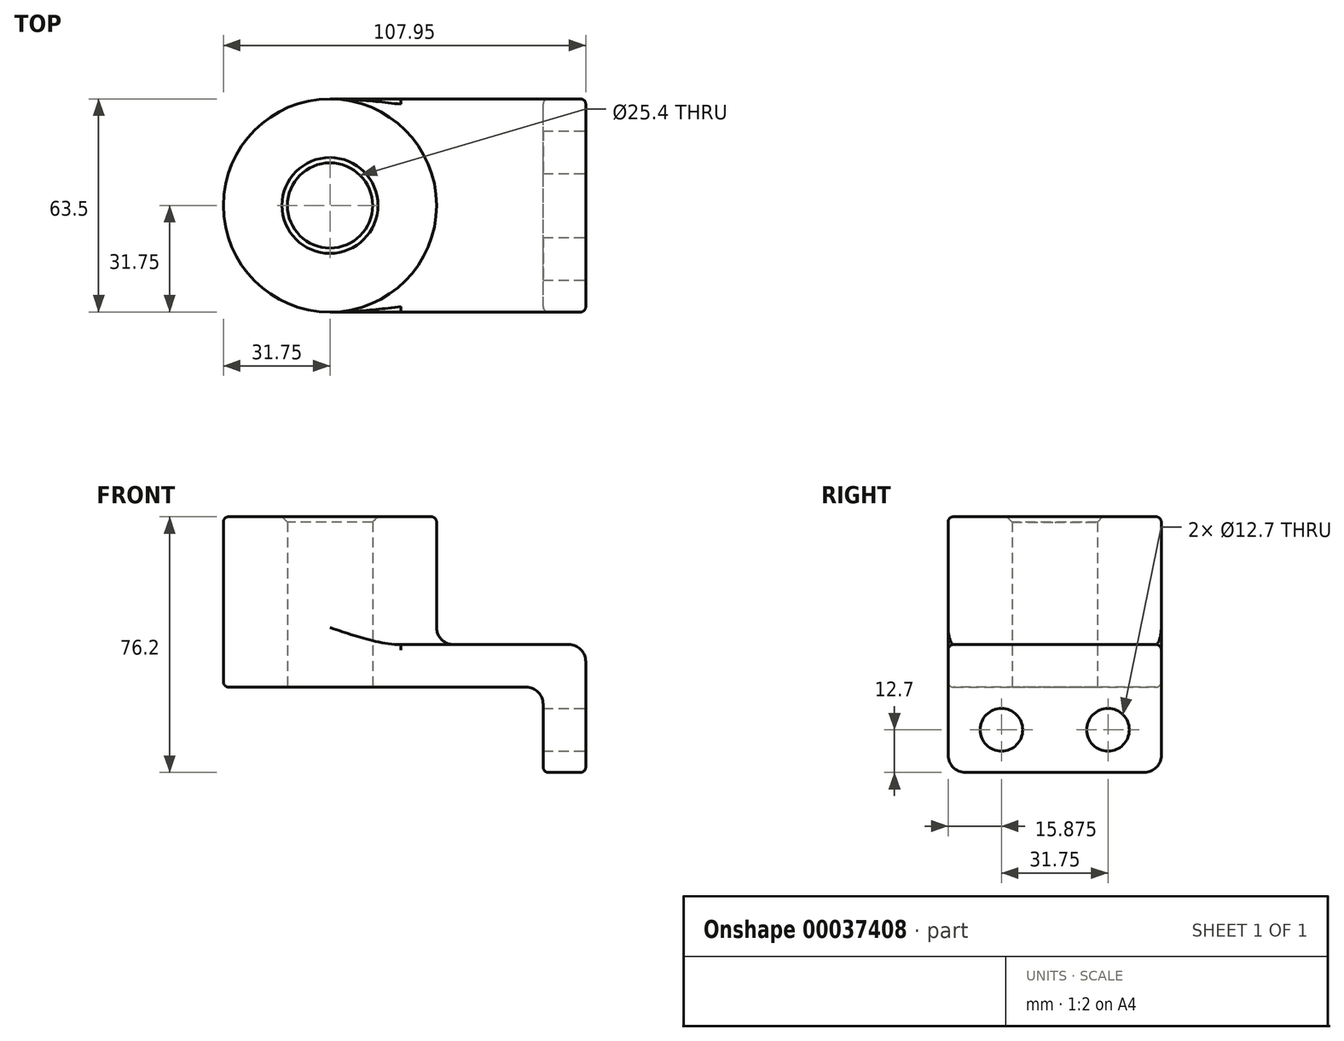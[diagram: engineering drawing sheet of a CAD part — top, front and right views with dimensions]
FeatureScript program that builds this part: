
annotation { "Feature Type Name" : "Feature", "Feature Type Description" : "" }
export const myFeature = defineFeature(function(context is Context, id is Id, definition is map)
    precondition{}
    {
        {
            var Q0;
            Q0=qCreatedBy(makeId("Top.planeOp"),FACE);
            var sketch = newSketch(context, id + "F0", { "sketchPlane" : qUnion([Q0])});
            skLineSegment(sketch, "E0.rect.bottom", {"start": v(-38.1, 31.75) * mm, "end": v(38.1, 31.75) * mm});
            skLineSegment(sketch, "E0.rect.top", {"start": v(-38.1, -31.75) * mm, "end": v(38.1, -31.75) * mm});
            skLineSegment(sketch, "E0.rect.left", {"start": v(-38.1, 31.75) * mm, "end": v(-38.1, -31.75) * mm});
            skLineSegment(sketch, "E0.rect.right", {"start": v(38.1, 31.75) * mm, "end": v(38.1, -31.75) * mm});
            skPoint(sketch, "E0.rect.middle", {"position": v(0, 0) * mm});
            skCircle(sketch, "E1", {"center": v(-38.1, 0) * mm, "radius": 31.75 * mm});
            skCircle(sketch, "E2", {"center": v(-38.1, 0) * mm, "radius": 12.7 * mm});
            skSolve(sketch);
        }
        {
            var Q0;
            {var subQ3=sQuery(id+"F0.wireOp",EDGE,"E0.rect.bottom");Q0=makeQuery(id+"F0.imprint","IMPRINT",FACE,{"disambiguationData":[TD([[makeQuery(id+"F0.imprint","IMPRINT",EDGE,{"derivedFrom":subQ3}),-1.0]])]});}
            var Q1;
            {var subQ0=sQuery(id+"F0.wireOp",EDGE,"E2");var subQ1=sQuery(id+"F0.wireOp",EDGE,"E0.rect.left");var subQ3=makeQuery(id+"F0.imprint","INTERSECT",VERTEX,{"disambiguationData":[OD(0.0)],"derivedFrom":[subQ1,subQ0]});Q1=makeQuery(id+"F0.imprint","IMPRINT",FACE,{"disambiguationData":[TD([[makeQuery(id+"F0.imprint","IMPRINT",EDGE,{"disambiguationData":[TD([[subQ3,1.0]])],"derivedFrom":subQ0}),-1.0]])]});}
            var Q2;
            {var subQ0=sQuery(id+"F0.wireOp",EDGE,"E2");var subQ1=sQuery(id+"F0.wireOp",EDGE,"E0.rect.left");var subQ3=makeQuery(id+"F0.imprint","INTERSECT",VERTEX,{"disambiguationData":[OD(0.0)],"derivedFrom":[subQ1,subQ0]});Q2=makeQuery(id+"F0.imprint","IMPRINT",FACE,{"disambiguationData":[TD([[makeQuery(id+"F0.imprint","IMPRINT",EDGE,{"disambiguationData":[TD([[subQ3,-1.0]])],"derivedFrom":subQ0}),-1.0]])]});}
            extrude(context, id + "F1", {"entities" : qUnion([Q0, Q1, Q2]), "depth" : 12.7 * mm});
        }
        {
            var Q0;
            {var subQ0=sQuery(id+"F0.wireOp",EDGE,"E2");var subQ1=sQuery(id+"F0.wireOp",EDGE,"E0.rect.left");var subQ3=makeQuery(id+"F0.imprint","INTERSECT",VERTEX,{"disambiguationData":[OD(0.0)],"derivedFrom":[subQ1,subQ0]});Q0=makeQuery(id+"F0.imprint","IMPRINT",FACE,{"disambiguationData":[TD([[makeQuery(id+"F0.imprint","IMPRINT",EDGE,{"disambiguationData":[TD([[subQ3,1.0]])],"derivedFrom":subQ0}),-1.0]])]});}
            var Q1;
            {var subQ0=sQuery(id+"F0.wireOp",EDGE,"E2");var subQ1=sQuery(id+"F0.wireOp",EDGE,"E0.rect.left");var subQ3=makeQuery(id+"F0.imprint","INTERSECT",VERTEX,{"disambiguationData":[OD(0.0)],"derivedFrom":[subQ1,subQ0]});Q1=makeQuery(id+"F0.imprint","IMPRINT",FACE,{"disambiguationData":[TD([[makeQuery(id+"F0.imprint","IMPRINT",EDGE,{"disambiguationData":[TD([[subQ3,-1.0]])],"derivedFrom":subQ0}),-1.0]])]});}
            extrude(context, id + "F2", {"entities" : qUnion([Q0, Q1]), "operationType" : NewBodyOperationType.ADD, "depth" : 50.8 * mm});
        }
        {
            var Q0;
            Q0=makeQuery(id+"F1.opExtrude","SWEPT_FACE",FACE,{"disambiguationData":[OSD([sQuery(id+"F0.wireOp",EDGE,"E0.rect.right")])]});
            var sketch = newSketch(context, id + "F3", { "sketchPlane" : qUnion([Q0])});
            skLineSegment(sketch, "E3.bottom", {"start": v(-31.75, 12.7) * mm, "end": v(31.75, 12.7) * mm});
            skLineSegment(sketch, "E3.top", {"start": v(-31.75, -25.4) * mm, "end": v(31.75, -25.4) * mm});
            skLineSegment(sketch, "E3.left", {"start": v(-31.75, 12.7) * mm, "end": v(-31.75, -25.4) * mm});
            skLineSegment(sketch, "E3.right", {"start": v(31.75, 12.7) * mm, "end": v(31.75, -25.4) * mm});
            skLineSegment(sketch, "E4", {"start": v(0, 0) * mm, "end": v(0, -25.4) * mm, "construction": true});
            skCircle(sketch, "E5", {"center": v(-15.87, -12.7) * mm, "radius": 6.35 * mm});
            skCircle(sketch, "E6.MirrorC", {"center": v(15.88, -12.7) * mm, "radius": 6.35 * mm});
            skSolve(sketch);
        }
        {
            var Q0;
            {var subQ2=sQuery(id+"F3.wireOp",EDGE,"E3.top");Q0=makeQuery(id+"F3.imprint","IMPRINT",FACE,{"disambiguationData":[TD([[makeQuery(id+"F3.imprint","IMPRINT",EDGE,{"derivedFrom":subQ2}),1.0]])]});}
            var Q1;
            {var subQ2=sQuery(id+"F3.wireOp",EDGE,"E3.bottom");Q1=makeQuery(id+"F3.imprint","IMPRINT",FACE,{"disambiguationData":[TD([[makeQuery(id+"F3.imprint","IMPRINT",EDGE,{"derivedFrom":subQ2}),1.0]])]});}
            extrude(context, id + "F4", {"entities" : qUnion([Q0, Q1]), "operationType" : NewBodyOperationType.ADD, "oppositeDirection" : true, "depth" : 12.7 * mm});
        }
        {
            var Q0;
            {var subQ0=sQuery(id+"F0.wireOp",EDGE,"E1");Q0=makeQuery(id+"F2.boolean.opBoolean","INTERSECT",EDGE,{"derivedFrom":[makeQuery(id+"F1.opExtrude","CAP_FACE",FACE,{"disambiguationData":[OSD([sQuery(id+"F0.wireOp",EDGE,"E0.rect.bottom"),sQuery(id+"F0.wireOp",EDGE,"E0.rect.top"),sQuery(id+"F0.wireOp",EDGE,"E0.rect.right"),subQ0,sQuery(id+"F0.wireOp",EDGE,"E2")])],"isStart":false}),makeQuery(id+"F2.opExtrude","SWEPT_FACE",FACE,{"disambiguationData":[OSD([subQ0])]})]});}
            var Q1;
            Q1=makeQuery(id+"F4.opExtrude","SWEPT_EDGE",EDGE,{"disambiguationData":[OSD([sQuery(id+"F3.wireOp",EDGE,"E3.top"),sQuery(id+"F3.wireOp",EDGE,"E3.left")])]});
            var Q2;
            Q2=makeQuery(id+"F4.opExtrude","SWEPT_EDGE",EDGE,{"disambiguationData":[OSD([sQuery(id+"F3.wireOp",EDGE,"E3.top"),sQuery(id+"F3.wireOp",EDGE,"E3.right")])]});
            var Q3;
            Q3=makeQuery(id+"F1.opExtrude","CAP_EDGE",EDGE,{"disambiguationData":[OSD([sQuery(id+"F0.wireOp",EDGE,"E0.rect.right")])],"isStart":false});
            var Q4;
            Q4=makeQuery(id+"F4.boolean.opBoolean","INTERSECT",EDGE,{"derivedFrom":[makeQuery(id+"F1.opExtrude","CAP_FACE",FACE,{"disambiguationData":[OSD([sQuery(id+"F0.wireOp",EDGE,"E0.rect.bottom"),sQuery(id+"F0.wireOp",EDGE,"E0.rect.top"),sQuery(id+"F0.wireOp",EDGE,"E0.rect.right"),sQuery(id+"F0.wireOp",EDGE,"E1"),sQuery(id+"F0.wireOp",EDGE,"E2")])],"isStart":true}),makeQuery(id+"F4.opExtrude","CAP_FACE",FACE,{"disambiguationData":[OSD([sQuery(id+"F3.wireOp",EDGE,"E3.bottom"),sQuery(id+"F3.wireOp",EDGE,"E3.top"),sQuery(id+"F3.wireOp",EDGE,"E3.left"),sQuery(id+"F3.wireOp",EDGE,"E3.right"),sQuery(id+"F3.wireOp",EDGE,"E5"),sQuery(id+"F3.wireOp",EDGE,"E6.MirrorC")])],"isStart":false})]});
            fillet(context, id + "F5", {"entities" : qUnion([Q0, Q1, Q2, Q3, Q4]), "radius" : 5.08 * mm, "tangentPropagation" : true, "allowEdgeOverflow" : false});
        }
        {
            var Q0;
            Q0=makeQuery(id+"F1.opExtrude","CAP_EDGE",EDGE,{"disambiguationData":[OSD([sQuery(id+"F0.wireOp",EDGE,"E0.rect.top")])],"isStart":false});
            var Q1;
            Q1=makeQuery(id+"F1.opExtrude","CAP_EDGE",EDGE,{"disambiguationData":[OSD([sQuery(id+"F0.wireOp",EDGE,"E0.rect.top")])],"isStart":true});
            var Q2;
            Q2=makeQuery(id+"F2.opExtrude","CAP_EDGE",EDGE,{"disambiguationData":[OSD([sQuery(id+"F0.wireOp",EDGE,"E1")])],"isStart":false});
            fillet(context, id + "F6", {"entities" : qUnion([Q0, Q1, Q2]), "radius" : 1.59 * mm, "tangentPropagation" : true, "allowEdgeOverflow" : false});
        }
        {
            var Q0;
            Q0=makeQuery(id+"F2.opExtrude","CAP_EDGE",EDGE,{"disambiguationData":[OSD([sQuery(id+"F0.wireOp",EDGE,"E2")])],"isStart":false});
            chamfer(context, id + "F7", {"entities" : qUnion([Q0]), "width" : 1.59 * mm, "tangentPropagation" : true});
        }
    });
